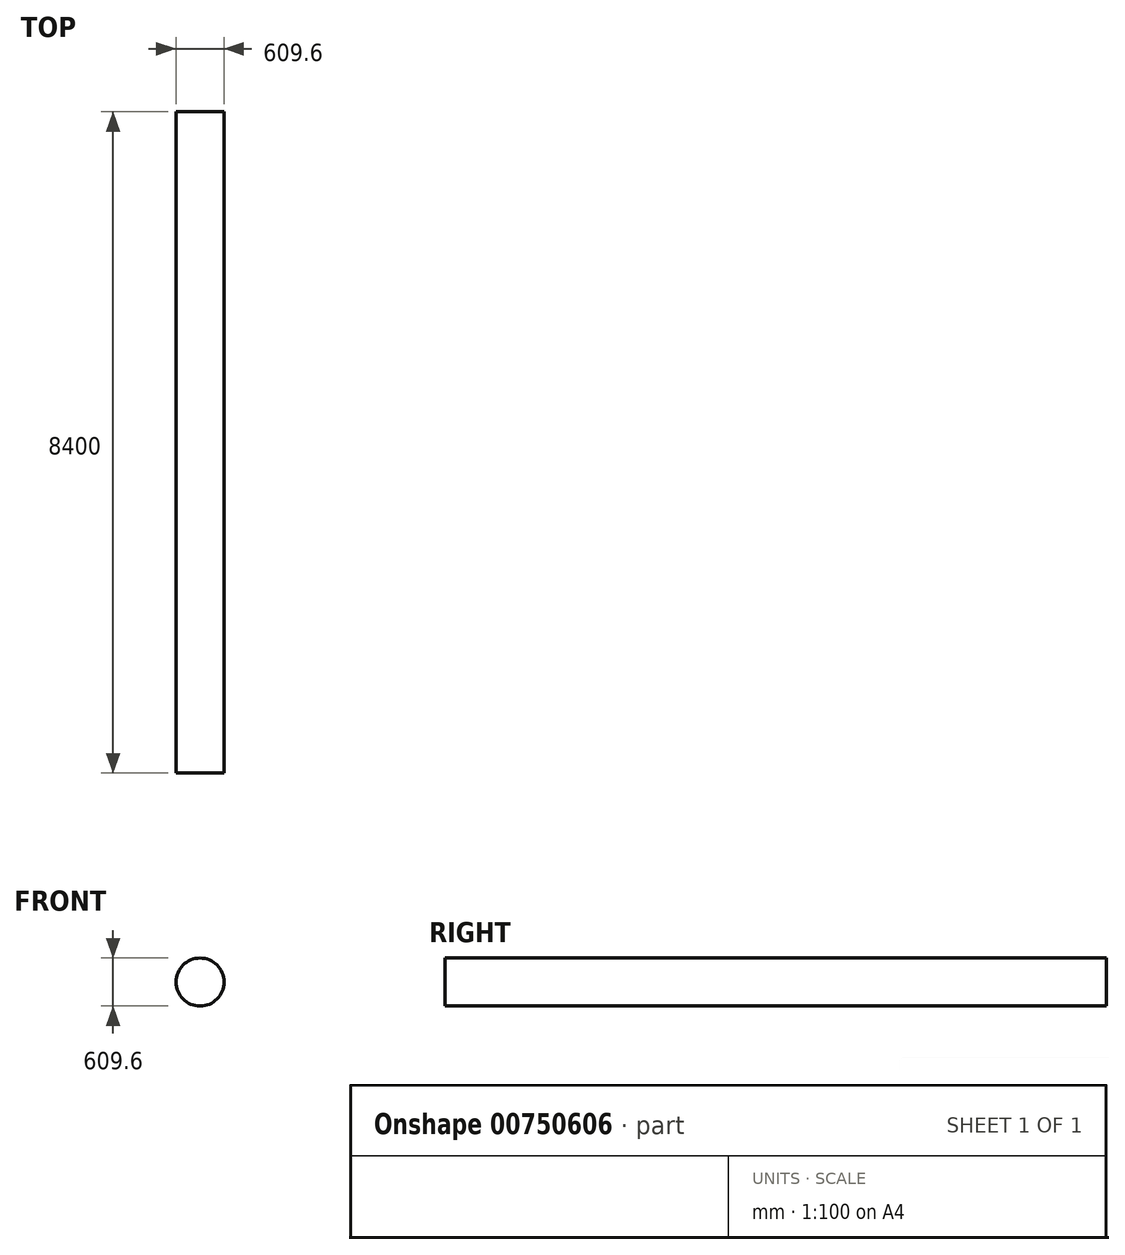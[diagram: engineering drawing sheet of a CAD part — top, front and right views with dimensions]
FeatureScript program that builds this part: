
annotation { "Feature Type Name" : "Feature", "Feature Type Description" : "" }
export const myFeature = defineFeature(function(context is Context, id is Id, definition is map)
    precondition{}
    {
        {
            var Q0;
            Q0=qCreatedBy(makeId("Front.planeOp"),FACE);
            var sketch = newSketch(context, id + "F0", { "sketchPlane" : qUnion([Q0])});
            skCircle(sketch, "E0", {"center": v(0, 0) * mm, "radius": 304.8 * mm});
            skSolve(sketch);
        }
        {
            var Q0;
            Q0 = qSketchRegion(id + "F0", true);
            extrude(context, id + "F1", {"entities" : qUnion([Q0]), "depth" : 8400 * mm, "offsetDistance" : 25.4 * mm});
        }
    });
